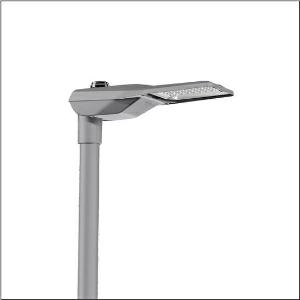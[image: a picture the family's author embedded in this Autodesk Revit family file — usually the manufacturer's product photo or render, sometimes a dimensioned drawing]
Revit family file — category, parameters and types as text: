
# Revit family: streetlight_sl_21_mini___st0_8a_5xe6c47n08jb_51ba
name_source: partatom
category: Lighting Fixtures
units: mm (PartAtom-declared; Revit-internal decimal feet)

## family parameters
Cut with Voids When Loaded = No
Host = Face
Light Source = No
Part Type = Normal
Room Calculation Point = No
Round Connector Dimension = Use Diameter
Shared = No

## types (1)
- --- (1 x LED, 13390 lm, 87.3 W, 4000K)
    Apparent Load = 87 VA
    CIE Flux Codes = 41 75 97 100 100
    Color Rendering = 70
    Color Temperature = 4000K
    Default Elevation = 1800 mm
    Description = Streetlight SL 21 mini, mast luminaire, primary light control with lens, of PMMA, primary optical cover: cover, of toughened safety glass, transparent, light distribution: ST0.8a, light emission: direct distribution, primary light characteristic: asymmetric, installation type: side-entry, LED, 3G 2.5mm², High Power LED, rated luminous flux: 13.390lm, luminous efficacy: 153lm/W, light colour: 740, colour temperature: 4000K, control: overheat protection, pre-setting: linear dimming characteristic, constant luminous flux control, time-dependent luminous flux control, flexible luminous flux parameterisation, mains connection: 230..240V, AC, 50/60Hz, connection cable pre-assembled, cable length: 10,5m, wiring characteristics: H05VV-F, start of lifetime: 87W, end of service life: 90W, reduction: 40W, luminaire housing, of diecast aluminium (EN AC-44300), powder-coated, Siteco® metallic grey (DB 702S), corrosivity category C5 mid according to DIN EN ISO 12944, multi-level sealing system, sealing non-destructively replaceable, inclination adjustable: 0°, 5°, 10°, 15°, length: 628mm, width: 235mm, height: 110mm, spigot size: 42mm (side-entry), protection rating (complete): IP66, insulation class (complete): insulation class I (protective earthing), certification: CE, ENEC, ENEC+, VDE, impact resistance: IK09, permissible operating ambient temperature for outdoor applications: -40..+50°C, standard-compliant lighting for roads and squares, packaging unit: 1 piece

Light Distribution: ST0.8a
    Height = 110 mm
    Lamp = 1 x LED
    Lamp Light Flux = 13390 lm
    Lamp Power = 87.3 W
    Lamp count = 1
    Length = 625 mm
    Luminous efficacy = 153 lm/W
    Manufacturer = Siteco
    ModVariant = No
    Model = 5XE6C47N08JB
    Number of Poles = 1
    OnlyDefault = Yes
    Power Factor = 1
    Product Name = Streetlight SL 21 mini | ST0.8a
    Product group = mast luminaire | pylon top
    ProductGroupID = 6100
    Protection Class = Protection class I
    Protection Degree = IP 66
    RLX_Detail_Level = 1
    RLX_Emergency_Light_Flux = 0 lm
    RLX_Emergency_Type = 0
    RLX_Emergency_Type_DB = No
    RlxData = <blob elided: 92013 chars, md5=fcf544d2>
    Socket = socket
    Standby Power = 0 W
    System Light Flux = 13390 lm
    System Power = 87 W
    Type Comments = factory setting: luminous flux: 100 % | dim-lin: 254 | 915 mA
    Type Image = l_1294379.jpg
    URL = http://relux.com
    VarID = @adj_103715
    Voltage = 0 V
    Weight = 0.00 kg
    Width = 234 mm

## geometry (parser evidence)
native form markers: Blend x4, Sweep x12
no freeform markers — native parametric forms only
